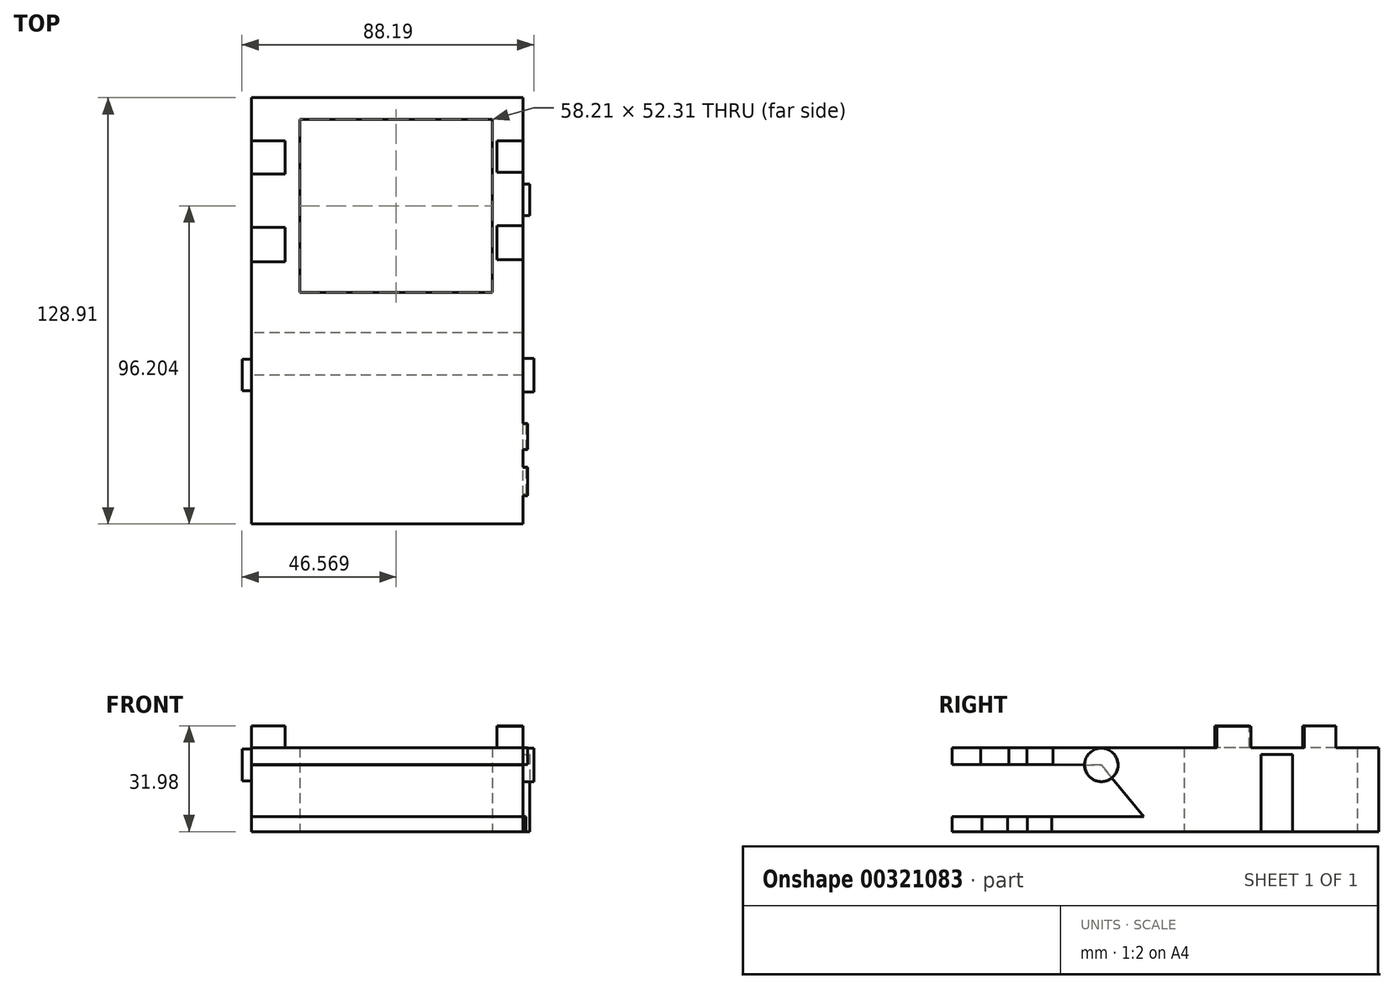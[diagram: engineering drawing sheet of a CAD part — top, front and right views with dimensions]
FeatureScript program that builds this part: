
annotation { "Feature Type Name" : "Feature", "Feature Type Description" : "" }
export const myFeature = defineFeature(function(context is Context, id is Id, definition is map)
    precondition{}
    {
        {
            var Q0;
            Q0=qCreatedBy(makeId("Top.planeOp"),FACE);
            var sketch = newSketch(context, id + "F0", { "sketchPlane" : qUnion([Q0])});
            skLineSegment(sketch, "E0.bottom", {"start": v(-32.04, 58.86) * mm, "end": v(50, 58.86) * mm});
            skLineSegment(sketch, "E0.top", {"start": v(-32.04, -70.05) * mm, "end": v(50, -70.05) * mm});
            skLineSegment(sketch, "E0.left", {"start": v(-32.04, 58.86) * mm, "end": v(-32.04, -70.05) * mm});
            skLineSegment(sketch, "E0.right", {"start": v(50, 58.86) * mm, "end": v(50, -70.05) * mm});
            skLineSegment(sketch, "E1.bottom", {"start": v(-20.73, 52.3) * mm, "end": v(40.76, 52.3) * mm});
            skLineSegment(sketch, "E1.top", {"start": v(-20.73, 0) * mm, "end": v(40.76, 0) * mm});
            skLineSegment(sketch, "E1.left", {"start": v(-20.73, 52.3) * mm, "end": v(-20.73, 0) * mm});
            skLineSegment(sketch, "E1.right", {"start": v(40.76, 52.3) * mm, "end": v(40.76, 0) * mm});
            skSolve(sketch);
        }
        {
            var Q0;
            Q0 = qSketchRegion(id + "F0", true);
            extrude(context, id + "F1", {"entities" : qUnion([Q0]), "depth" : 25.4 * mm});
        }
        {
            var Q0;
            Q0=makeQuery(id+"F1.opExtrude","SWEPT_FACE",FACE,{"disambiguationData":[OSD([sQuery(id+"F0.wireOp",EDGE,"E0.left")])]});
            var sketch = newSketch(context, id + "F2", { "sketchPlane" : qUnion([Q0])});
            skLineSegment(sketch, "E2", {"start": v(70.05, 20.26) * mm, "end": v(70.05, 4.58) * mm});
            skLineSegment(sketch, "E3", {"start": v(70.05, 4.58) * mm, "end": v(12.17, 4.58) * mm});
            skLineSegment(sketch, "E4", {"start": v(25, 20.16) * mm, "end": v(70.05, 20.26) * mm});
            skLineSegment(sketch, "E5", {"start": v(12.17, 4.58) * mm, "end": v(25, 20.16) * mm});
            skSolve(sketch);
        }
        {
            var Q0;
            Q0 = qSketchRegion(id + "F2", true);
            extrude(context, id + "F3", {"entities" : qUnion([Q0]), "operationType" : NewBodyOperationType.REMOVE, "oppositeDirection" : true, "depth" : 103.34 * mm});
        }
        {
            var Q0;
            Q0=makeQuery(id+"F1.opExtrude","SWEPT_FACE",FACE,{"disambiguationData":[OSD([sQuery(id+"F0.wireOp",EDGE,"E0.left")])]});
            var sketch = newSketch(context, id + "F4", { "sketchPlane" : qUnion([Q0])});
            skLineSegment(sketch, "E6.bottom", {"start": v(-45.84, 25.4) * mm, "end": v(-35.86, 25.4) * mm});
            skLineSegment(sketch, "E6.top", {"start": v(-45.84, 31.97) * mm, "end": v(-35.86, 31.97) * mm});
            skLineSegment(sketch, "E6.left", {"start": v(-45.84, 25.4) * mm, "end": v(-45.84, 31.97) * mm});
            skLineSegment(sketch, "E6.right", {"start": v(-35.86, 25.4) * mm, "end": v(-35.86, 31.97) * mm});
            skLineSegment(sketch, "E7.bottom", {"start": v(-19.66, 25.4) * mm, "end": v(-9.28, 25.4) * mm});
            skLineSegment(sketch, "E7.top", {"start": v(-19.66, 31.98) * mm, "end": v(-9.28, 31.98) * mm});
            skLineSegment(sketch, "E7.left", {"start": v(-19.66, 25.4) * mm, "end": v(-19.66, 31.98) * mm});
            skLineSegment(sketch, "E7.right", {"start": v(-9.28, 25.4) * mm, "end": v(-9.28, 31.98) * mm});
            skSolve(sketch);
        }
        {
            var Q0;
            Q0=makeQuery(id+"F4.imprint","IMPRINT",FACE,{"disambiguationData":[TD([[makeQuery(id+"F4.imprint","IMPRINT",EDGE,{"derivedFrom":sQuery(id+"F4.wireOp",EDGE,"E6.bottom")}),1.0]])]});
            var Q1;
            Q1=makeQuery(id+"F4.imprint","IMPRINT",FACE,{"disambiguationData":[TD([[makeQuery(id+"F4.imprint","IMPRINT",EDGE,{"derivedFrom":sQuery(id+"F4.wireOp",EDGE,"E7.bottom")}),1.0]])]});
            extrude(context, id + "F5", {"entities" : qUnion([Q0, Q1]), "operationType" : NewBodyOperationType.ADD, "oppositeDirection" : true, "depth" : 10.16 * mm});
        }
        {
            var Q0;
            Q0=makeQuery(id+"F1.opExtrude","SWEPT_FACE",FACE,{"disambiguationData":[OSD([sQuery(id+"F0.wireOp",EDGE,"E0.right")])]});
            var sketch = newSketch(context, id + "F6", { "sketchPlane" : qUnion([Q0])});
            skLineSegment(sketch, "E8.bottom", {"start": v(9.95, 25.4) * mm, "end": v(20.24, 25.4) * mm});
            skLineSegment(sketch, "E8.top", {"start": v(9.95, 31.86) * mm, "end": v(20.24, 31.86) * mm});
            skLineSegment(sketch, "E8.left", {"start": v(9.95, 25.4) * mm, "end": v(9.95, 31.86) * mm});
            skLineSegment(sketch, "E8.right", {"start": v(20.24, 25.4) * mm, "end": v(20.24, 31.86) * mm});
            skSolve(sketch);
        }
        {
            var Q0;
            {var subQ5=sQuery(id+"F6.wireOp",EDGE,"E8.bottom");Q0=makeQuery(id+"F6.imprint","IMPRINT",FACE,{"disambiguationData":[TD([[makeQuery(id+"F6.imprint","IMPRINT",EDGE,{"derivedFrom":subQ5}),1.0]])]});}
            var sketch = newSketch(context, id + "F7", { "sketchPlane" : qUnion([Q0])});
            skLineSegment(sketch, "E9.bottom", {"start": v(36.31, 25.25) * mm, "end": v(45.88, 25.25) * mm});
            skLineSegment(sketch, "E9.top", {"start": v(36.31, 31.97) * mm, "end": v(45.88, 31.97) * mm});
            skLineSegment(sketch, "E9.left", {"start": v(36.31, 25.25) * mm, "end": v(36.31, 31.97) * mm});
            skLineSegment(sketch, "E9.right", {"start": v(45.88, 25.25) * mm, "end": v(45.88, 31.97) * mm});
            skSolve(sketch);
        }
        {
            var Q0;
            Q0=makeQuery(id+"F6.imprint","IMPRINT",FACE,{"disambiguationData":[TD([[makeQuery(id+"F6.imprint","IMPRINT",EDGE,{"derivedFrom":sQuery(id+"F6.wireOp",EDGE,"E8.bottom")}),-1.0]])]});
            var Q1;
            {var subQ0=sQuery(id+"F7.wireOp",EDGE,"E9.top");Q1=makeQuery(id+"F7.imprint","IMPRINT",FACE,{"disambiguationData":[TD([[makeQuery(id+"F7.imprint","IMPRINT",EDGE,{"derivedFrom":subQ0}),-1.0]])]});}
            extrude(context, id + "F8", {"entities" : qUnion([Q0, Q1]), "operationType" : NewBodyOperationType.ADD, "oppositeDirection" : true, "depth" : 7.92 * mm});
        }
        {
            var Q0;
            {var subQ0=sQuery(id+"F0.wireOp",EDGE,"E0.right");Q0=makeQuery(id+"F8.boolean.opBoolean","MERGE",FACE,{"derivedFrom":[makeQuery(id+"F1.opExtrude","SWEPT_FACE",FACE,{"disambiguationData":[OSD([subQ0])]}),makeQuery(id+"F8.opExtrude","CAP_FACE",FACE,{"disambiguationData":[OSD([sQuery(id+"F6.wireOp",EDGE,"E8.bottom"),sQuery(id+"F6.wireOp",EDGE,"E8.top"),sQuery(id+"F6.wireOp",EDGE,"E8.left"),sQuery(id+"F6.wireOp",EDGE,"E8.right")])],"isStart":true}),makeQuery(id+"F8.opExtrude","CAP_FACE",FACE,{"disambiguationData":[OSD([subQ0,sQuery(id+"F7.wireOp",EDGE,"E9.top"),sQuery(id+"F7.wireOp",EDGE,"E9.left"),sQuery(id+"F7.wireOp",EDGE,"E9.right")])],"isStart":true})]});}
            var sketch = newSketch(context, id + "F9", { "sketchPlane" : qUnion([Q0])});
            skLineSegment(sketch, "E10.bottom", {"start": v(-47.52, 20.2) * mm, "end": v(-47.52, 20.2) * mm});
            skLineSegment(sketch, "E10.top", {"start": v(-47.52, 20.2) * mm, "end": v(-47.52, 20.2) * mm});
            skLineSegment(sketch, "E10.left", {"start": v(-47.52, 20.2) * mm, "end": v(-47.52, 20.2) * mm});
            skLineSegment(sketch, "E10.right", {"start": v(-47.52, 20.2) * mm, "end": v(-47.52, 20.2) * mm});
            skLineSegment(sketch, "E11.bottom", {"start": v(-47.52, 20.2) * mm, "end": v(-39.6, 20.2) * mm});
            skLineSegment(sketch, "E11.top", {"start": v(-47.52, 25.4) * mm, "end": v(-39.6, 25.4) * mm});
            skLineSegment(sketch, "E11.left", {"start": v(-47.52, 20.2) * mm, "end": v(-47.52, 25.4) * mm});
            skLineSegment(sketch, "E11.right", {"start": v(-39.6, 20.2) * mm, "end": v(-39.6, 25.4) * mm});
            skLineSegment(sketch, "E12.bottom", {"start": v(-61.46, 20.24) * mm, "end": v(-52.9, 20.24) * mm});
            skLineSegment(sketch, "E12.top", {"start": v(-61.46, 25.4) * mm, "end": v(-52.9, 25.4) * mm});
            skLineSegment(sketch, "E12.left", {"start": v(-61.46, 20.24) * mm, "end": v(-61.46, 25.4) * mm});
            skLineSegment(sketch, "E12.right", {"start": v(-52.9, 20.24) * mm, "end": v(-52.9, 25.4) * mm});
            skSolve(sketch);
        }
        {
            var Q0;
            Q0=makeQuery(id+"F9.imprint","IMPRINT",FACE,{"disambiguationData":[TD([[makeQuery(id+"F9.imprint","IMPRINT",EDGE,{"derivedFrom":sQuery(id+"F9.wireOp",EDGE,"E12.bottom")}),1.0]])]});
            var Q1;
            Q1=makeQuery(id+"F9.imprint","IMPRINT",FACE,{"disambiguationData":[TD([[makeQuery(id+"F9.imprint","IMPRINT",EDGE,{"derivedFrom":sQuery(id+"F9.wireOp",EDGE,"E11.bottom")}),1.0]])]});
            extrude(context, id + "F10", {"entities" : qUnion([Q0, Q1]), "operationType" : NewBodyOperationType.ADD, "depth" : 1.34 * mm});
        }
        {
            var Q0;
            {var subQ0=sQuery(id+"F6.wireOp",EDGE,"E8.right");var subQ1=sQuery(id+"F6.wireOp",EDGE,"E8.left");var subQ2=sQuery(id+"F6.wireOp",EDGE,"E8.top");var subQ3=makeQuery(id+"F8.opExtrude","CAP_FACE",FACE,{"disambiguationData":[OSD([sQuery(id+"F6.wireOp",EDGE,"E8.bottom"),subQ2,subQ1,subQ0])],"isStart":true});var subQ4=sQuery(id+"F0.wireOp",EDGE,"E0.top");var subQ5=sQuery(id+"F0.wireOp",EDGE,"E0.right");var subQ6=makeQuery(id+"F1.opExtrude","SWEPT_FACE",FACE,{"disambiguationData":[OSD([subQ5])]});var subQ7=sQuery(id+"F0.wireOp",EDGE,"E0.bottom");var subQ8=sQuery(id+"F0.wireOp",EDGE,"E1.right");var subQ9=sQuery(id+"F0.wireOp",EDGE,"E1.left");var subQ10=sQuery(id+"F0.wireOp",EDGE,"E1.top");var subQ11=sQuery(id+"F0.wireOp",EDGE,"E1.bottom");var subQ12=sQuery(id+"F0.wireOp",EDGE,"E0.left");var subQ13=sQuery(id+"F7.wireOp",EDGE,"E9.top");var subQ14=sQuery(id+"F7.wireOp",EDGE,"E9.right");var subQ15=sQuery(id+"F7.wireOp",EDGE,"E9.left");var subQ16=makeQuery(id+"F8.opExtrude","CAP_FACE",FACE,{"disambiguationData":[OSD([subQ5,subQ13,subQ15,subQ14])],"isStart":true});Q0=makeQuery(id+"F10.boolean.opBoolean","SPLIT",FACE,{"disambiguationData":[TD([makeQuery(id+"F1.opExtrude","SWEPT_FACE",FACE,{"disambiguationData":[OSD([subQ7])]}),makeQuery(id+"F1.opExtrude","CAP_FACE",FACE,{"disambiguationData":[OSD([subQ7,subQ4,subQ12,subQ5,subQ11,subQ10,subQ9,subQ8])],"isStart":true}),makeQuery(id+"F1.opExtrude","CAP_FACE",FACE,{"disambiguationData":[OSD([subQ7,subQ4,subQ12,subQ5,subQ11,subQ10,subQ9,subQ8])],"isStart":false}),makeQuery(id+"F1.opExtrude","SWEPT_FACE",FACE,{"disambiguationData":[OSD([subQ4])]}),subQ6,makeQuery(id+"F3.boolean.opBoolean","COPY",FACE,{"derivedFrom":makeQuery(id+"F3.opExtrude","SWEPT_FACE",FACE,{"disambiguationData":[OSD([sQuery(id+"F2.wireOp",EDGE,"E3")])]})}),makeQuery(id+"F3.boolean.opBoolean","COPY",FACE,{"derivedFrom":makeQuery(id+"F3.opExtrude","SWEPT_FACE",FACE,{"disambiguationData":[OSD([sQuery(id+"F2.wireOp",EDGE,"E4")])]})}),makeQuery(id+"F3.boolean.opBoolean","COPY",FACE,{"derivedFrom":makeQuery(id+"F3.opExtrude","SWEPT_FACE",FACE,{"disambiguationData":[OSD([sQuery(id+"F2.wireOp",EDGE,"E5")])]})}),subQ3,makeQuery(id+"F8.opExtrude","SWEPT_FACE",FACE,{"disambiguationData":[OSD([subQ2])]}),makeQuery(id+"F8.opExtrude","SWEPT_FACE",FACE,{"disambiguationData":[OSD([subQ1])]}),makeQuery(id+"F8.opExtrude","SWEPT_FACE",FACE,{"disambiguationData":[OSD([subQ0])]}),makeQuery(id+"F8.opExtrude","SWEPT_FACE",FACE,{"disambiguationData":[OSD([subQ13])]}),subQ16,makeQuery(id+"F8.opExtrude","SWEPT_FACE",FACE,{"disambiguationData":[OSD([subQ15])]}),makeQuery(id+"F8.opExtrude","SWEPT_FACE",FACE,{"disambiguationData":[OSD([subQ14])]}),makeQuery(id+"F10.opExtrude","SWEPT_FACE",FACE,{"disambiguationData":[OSD([sQuery(id+"F9.wireOp",EDGE,"E11.bottom")])]}),makeQuery(id+"F10.opExtrude","SWEPT_FACE",FACE,{"disambiguationData":[OSD([sQuery(id+"F9.wireOp",EDGE,"E11.top")])]}),makeQuery(id+"F10.opExtrude","SWEPT_FACE",FACE,{"disambiguationData":[OSD([sQuery(id+"F9.wireOp",EDGE,"E11.left")])]}),makeQuery(id+"F10.opExtrude","SWEPT_FACE",FACE,{"disambiguationData":[OSD([sQuery(id+"F9.wireOp",EDGE,"E11.right")])]}),makeQuery(id+"F10.opExtrude","SWEPT_FACE",FACE,{"disambiguationData":[OSD([sQuery(id+"F9.wireOp",EDGE,"E12.top")])]})])],"derivedFrom":makeQuery(id+"F8.boolean.opBoolean","MERGE",FACE,{"derivedFrom":[subQ6,subQ3,subQ16]})});}
            var sketch = newSketch(context, id + "F11", { "sketchPlane" : qUnion([Q0])});
            skLineSegment(sketch, "E13.bottom", {"start": v(-61.02, 4.58) * mm, "end": v(-53.28, 4.58) * mm});
            skLineSegment(sketch, "E13.top", {"start": v(-61.02, 0) * mm, "end": v(-53.28, 0) * mm});
            skLineSegment(sketch, "E13.left", {"start": v(-61.02, 4.58) * mm, "end": v(-61.02, 0) * mm});
            skLineSegment(sketch, "E13.right", {"start": v(-53.28, 4.58) * mm, "end": v(-53.28, 0) * mm});
            skLineSegment(sketch, "E14.bottom", {"start": v(-47.38, 4.58) * mm, "end": v(-39.97, 4.58) * mm});
            skLineSegment(sketch, "E14.top", {"start": v(-47.38, 0) * mm, "end": v(-39.97, 0) * mm});
            skLineSegment(sketch, "E14.left", {"start": v(-47.38, 4.58) * mm, "end": v(-47.38, 0) * mm});
            skLineSegment(sketch, "E14.right", {"start": v(-39.97, 4.58) * mm, "end": v(-39.97, 0) * mm});
            skSolve(sketch);
        }
        {
            var Q0;
            Q0=makeQuery(id+"F11.imprint","IMPRINT",FACE,{"disambiguationData":[TD([[makeQuery(id+"F11.imprint","IMPRINT",EDGE,{"derivedFrom":sQuery(id+"F11.wireOp",EDGE,"E13.bottom")}),1.0]])]});
            var Q1;
            Q1=makeQuery(id+"F11.imprint","IMPRINT",FACE,{"disambiguationData":[TD([[makeQuery(id+"F11.imprint","IMPRINT",EDGE,{"derivedFrom":sQuery(id+"F11.wireOp",EDGE,"E14.bottom")}),1.0]])]});
            extrude(context, id + "F12", {"entities" : qUnion([Q0, Q1]), "operationType" : NewBodyOperationType.ADD, "depth" : 0.9 * mm});
        }
        {
            var Q0;
            Q0=makeQuery(id+"F5.boolean.opBoolean","MERGE",FACE,{"derivedFrom":[makeQuery(id+"F1.opExtrude","SWEPT_FACE",FACE,{"disambiguationData":[OSD([sQuery(id+"F0.wireOp",EDGE,"E0.left")])]}),makeQuery(id+"F5.opExtrude","CAP_FACE",FACE,{"disambiguationData":[OSD([sQuery(id+"F4.wireOp",EDGE,"E6.bottom"),sQuery(id+"F4.wireOp",EDGE,"E6.top"),sQuery(id+"F4.wireOp",EDGE,"E6.left"),sQuery(id+"F4.wireOp",EDGE,"E6.right")])],"isStart":true}),makeQuery(id+"F5.opExtrude","CAP_FACE",FACE,{"disambiguationData":[OSD([sQuery(id+"F4.wireOp",EDGE,"E7.bottom"),sQuery(id+"F4.wireOp",EDGE,"E7.top"),sQuery(id+"F4.wireOp",EDGE,"E7.left"),sQuery(id+"F4.wireOp",EDGE,"E7.right")])],"isStart":true})]});
            var sketch = newSketch(context, id + "F13", { "sketchPlane" : qUnion([Q0])});
            skCircle(sketch, "E15", {"center": v(25, 20.16) * mm, "radius": 4.8 * mm});
            skSolve(sketch);
        }
        {
            var Q0;
            {var subQ0=sQuery(id+"F13.wireOp",EDGE,"E15");var subQ1=makeQuery(id+"F3.boolean.opBoolean","COPY",EDGE,{"derivedFrom":makeQuery(id+"F3.opExtrude","CAP_EDGE",EDGE,{"disambiguationData":[OSD([sQuery(id+"F2.wireOp",EDGE,"E4")])],"isStart":true})});var subQ2=makeQuery(id+"F13.imprint","INTERSECT",VERTEX,{"derivedFrom":[subQ1,subQ0]});Q0=makeQuery(id+"F13.imprint","IMPRINT",FACE,{"disambiguationData":[TD([[makeQuery(id+"F13.imprint","IMPRINT",EDGE,{"disambiguationData":[TD([[subQ2,-1.0]])],"derivedFrom":subQ0}),1.0]])]});}
            var Q1;
            {var subQ0=sQuery(id+"F13.wireOp",EDGE,"E15");var subQ1=makeQuery(id+"F3.boolean.opBoolean","COPY",EDGE,{"derivedFrom":makeQuery(id+"F3.opExtrude","CAP_EDGE",EDGE,{"disambiguationData":[OSD([sQuery(id+"F2.wireOp",EDGE,"E4")])],"isStart":true})});var subQ2=makeQuery(id+"F13.imprint","INTERSECT",VERTEX,{"derivedFrom":[subQ1,subQ0]});Q1=makeQuery(id+"F13.imprint","IMPRINT",FACE,{"disambiguationData":[TD([[makeQuery(id+"F13.imprint","IMPRINT",EDGE,{"disambiguationData":[TD([[subQ2,1.0]])],"derivedFrom":subQ0}),1.0]])]});}
            extrude(context, id + "F14", {"entities" : qUnion([Q0, Q1]), "operationType" : NewBodyOperationType.ADD, "depth" : 2.88 * mm});
        }
        {
            var Q0;
            {var subQ0=makeQuery(id+"F10.opExtrude","SWEPT_FACE",FACE,{"disambiguationData":[OSD([sQuery(id+"F9.wireOp",EDGE,"E11.right")])]});var subQ1=makeQuery(id+"F3.boolean.opBoolean","COPY",FACE,{"derivedFrom":makeQuery(id+"F3.opExtrude","SWEPT_FACE",FACE,{"disambiguationData":[OSD([sQuery(id+"F2.wireOp",EDGE,"E4")])]})});var subQ2=makeQuery(id+"F10.opExtrude","SWEPT_FACE",FACE,{"disambiguationData":[OSD([sQuery(id+"F9.wireOp",EDGE,"E11.left")])]});var subQ3=sQuery(id+"F7.wireOp",EDGE,"E9.right");var subQ4=makeQuery(id+"F8.opExtrude","SWEPT_FACE",FACE,{"disambiguationData":[OSD([subQ3])]});var subQ5=makeQuery(id+"F3.boolean.opBoolean","COPY",FACE,{"derivedFrom":makeQuery(id+"F3.opExtrude","SWEPT_FACE",FACE,{"disambiguationData":[OSD([sQuery(id+"F2.wireOp",EDGE,"E3")])]})});var subQ6=makeQuery(id+"F10.opExtrude","SWEPT_FACE",FACE,{"disambiguationData":[OSD([sQuery(id+"F9.wireOp",EDGE,"E11.top")])]});var subQ7=sQuery(id+"F7.wireOp",EDGE,"E9.left");var subQ8=makeQuery(id+"F8.opExtrude","SWEPT_FACE",FACE,{"disambiguationData":[OSD([subQ7])]});var subQ9=sQuery(id+"F0.wireOp",EDGE,"E0.right");var subQ10=makeQuery(id+"F1.opExtrude","SWEPT_FACE",FACE,{"disambiguationData":[OSD([subQ9])]});var subQ11=sQuery(id+"F7.wireOp",EDGE,"E9.top");var subQ12=makeQuery(id+"F8.opExtrude","CAP_FACE",FACE,{"disambiguationData":[OSD([subQ9,subQ11,subQ7,subQ3])],"isStart":true});var subQ13=makeQuery(id+"F10.opExtrude","SWEPT_FACE",FACE,{"disambiguationData":[OSD([sQuery(id+"F9.wireOp",EDGE,"E12.top")])]});var subQ14=makeQuery(id+"F8.opExtrude","SWEPT_FACE",FACE,{"disambiguationData":[OSD([subQ11])]});var subQ15=sQuery(id+"F0.wireOp",EDGE,"E1.right");var subQ16=sQuery(id+"F0.wireOp",EDGE,"E1.left");var subQ17=sQuery(id+"F0.wireOp",EDGE,"E1.top");var subQ18=sQuery(id+"F0.wireOp",EDGE,"E1.bottom");var subQ19=sQuery(id+"F0.wireOp",EDGE,"E0.left");var subQ20=sQuery(id+"F0.wireOp",EDGE,"E0.top");var subQ21=sQuery(id+"F0.wireOp",EDGE,"E0.bottom");var subQ22=makeQuery(id+"F1.opExtrude","CAP_FACE",FACE,{"disambiguationData":[OSD([subQ21,subQ20,subQ19,subQ9,subQ18,subQ17,subQ16,subQ15])],"isStart":false});var subQ23=makeQuery(id+"F10.opExtrude","SWEPT_FACE",FACE,{"disambiguationData":[OSD([sQuery(id+"F9.wireOp",EDGE,"E11.bottom")])]});var subQ24=sQuery(id+"F6.wireOp",EDGE,"E8.right");var subQ25=makeQuery(id+"F8.opExtrude","SWEPT_FACE",FACE,{"disambiguationData":[OSD([subQ24])]});var subQ26=makeQuery(id+"F1.opExtrude","CAP_FACE",FACE,{"disambiguationData":[OSD([subQ21,subQ20,subQ19,subQ9,subQ18,subQ17,subQ16,subQ15])],"isStart":true});var subQ27=sQuery(id+"F6.wireOp",EDGE,"E8.left");var subQ28=makeQuery(id+"F8.opExtrude","SWEPT_FACE",FACE,{"disambiguationData":[OSD([subQ27])]});var subQ29=makeQuery(id+"F1.opExtrude","SWEPT_FACE",FACE,{"disambiguationData":[OSD([subQ21])]});var subQ30=makeQuery(id+"F3.boolean.opBoolean","COPY",FACE,{"derivedFrom":makeQuery(id+"F3.opExtrude","SWEPT_FACE",FACE,{"disambiguationData":[OSD([sQuery(id+"F2.wireOp",EDGE,"E5")])]})});var subQ31=sQuery(id+"F6.wireOp",EDGE,"E8.top");var subQ32=makeQuery(id+"F8.opExtrude","SWEPT_FACE",FACE,{"disambiguationData":[OSD([subQ31])]});var subQ33=makeQuery(id+"F8.opExtrude","CAP_FACE",FACE,{"disambiguationData":[OSD([sQuery(id+"F6.wireOp",EDGE,"E8.bottom"),subQ31,subQ27,subQ24])],"isStart":true});Q0=makeQuery(id+"F12.boolean.opBoolean","SPLIT",FACE,{"disambiguationData":[TD([subQ29])],"derivedFrom":makeQuery(id+"F10.boolean.opBoolean","SPLIT",FACE,{"disambiguationData":[TD([subQ29,subQ26,subQ22,makeQuery(id+"F1.opExtrude","SWEPT_FACE",FACE,{"disambiguationData":[OSD([subQ20])]}),subQ10,subQ5,subQ1,subQ30,subQ33,subQ32,subQ28,subQ25,subQ14,subQ12,subQ8,subQ4,subQ23,subQ6,subQ2,subQ0,subQ13])],"derivedFrom":makeQuery(id+"F8.boolean.opBoolean","MERGE",FACE,{"derivedFrom":[subQ10,subQ33,subQ12]})})});}
            var sketch = newSketch(context, id + "F15", { "sketchPlane" : qUnion([Q0])});
            skCircle(sketch, "E16", {"center": v(-25, 20.16) * mm, "radius": 5.07 * mm});
            skSolve(sketch);
        }
        {
            var Q0;
            Q0 = qSketchRegion(id + "F15", true);
            var Q1;
            Q1=makeQuery(id+"F1.opExtrude","SWEPT_FACE",FACE,{"disambiguationData":[OSD([sQuery(id+"F0.wireOp",EDGE,"E1.left")])]});
            extrude(context, id + "F16", {"entities" : qUnion([Q0, Q1]), "operationType" : NewBodyOperationType.ADD, "depth" : 3.27 * mm});
        }
        {
            var Q0;
            {var subQ0=sQuery(id+"F0.wireOp",EDGE,"E1.left");Q0=makeQuery(id+"F16.boolean.opBoolean","MERGE",FACE,{"derivedFrom":[makeQuery(id+"F12.boolean.opBoolean","MERGE",FACE,{"derivedFrom":[makeQuery(id+"F1.opExtrude","CAP_FACE",FACE,{"disambiguationData":[OSD([sQuery(id+"F0.wireOp",EDGE,"E0.bottom"),sQuery(id+"F0.wireOp",EDGE,"E0.top"),sQuery(id+"F0.wireOp",EDGE,"E0.left"),sQuery(id+"F0.wireOp",EDGE,"E0.right"),sQuery(id+"F0.wireOp",EDGE,"E1.bottom"),sQuery(id+"F0.wireOp",EDGE,"E1.top"),subQ0,sQuery(id+"F0.wireOp",EDGE,"E1.right")])],"isStart":true}),makeQuery(id+"F12.opExtrude","SWEPT_FACE",FACE,{"disambiguationData":[OSD([sQuery(id+"F11.wireOp",EDGE,"E13.top")])]}),makeQuery(id+"F12.opExtrude","SWEPT_FACE",FACE,{"disambiguationData":[OSD([sQuery(id+"F11.wireOp",EDGE,"E14.top")])]})]}),makeQuery(id+"F16.opExtrude","SWEPT_FACE",FACE,{"disambiguationData":[OSD([subQ0]),TDD([makeQuery(id+"F1.opExtrude","CAP_EDGE",EDGE,{"disambiguationData":[OSD([subQ0])],"isStart":true})])]})]});}
            var sketch = newSketch(context, id + "F17", { "sketchPlane" : qUnion([Q0])});
            skLineSegment(sketch, "E17.bottom", {"start": v(50, -23.2) * mm, "end": v(52.01, -23.2) * mm});
            skLineSegment(sketch, "E17.top", {"start": v(50, -32.78) * mm, "end": v(52.01, -32.78) * mm});
            skLineSegment(sketch, "E17.left", {"start": v(50, -23.2) * mm, "end": v(50, -32.78) * mm});
            skLineSegment(sketch, "E17.right", {"start": v(52.01, -23.2) * mm, "end": v(52.01, -32.78) * mm});
            skSolve(sketch);
        }
        {
            var Q0;
            Q0 = qSketchRegion(id + "F17", true);
            extrude(context, id + "F18", {"entities" : qUnion([Q0]), "operationType" : NewBodyOperationType.ADD, "oppositeDirection" : true, "depth" : 23.35 * mm});
        }
    });
